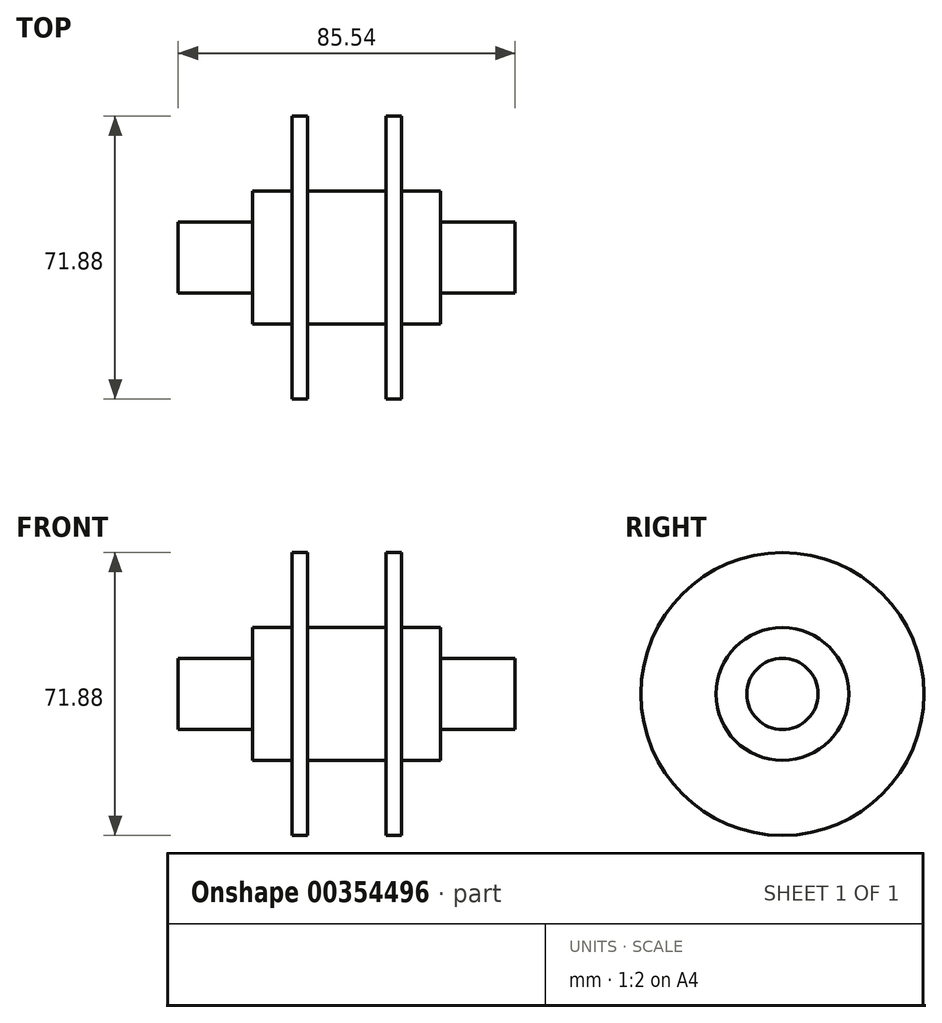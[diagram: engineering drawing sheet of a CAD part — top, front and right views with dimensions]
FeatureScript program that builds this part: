
annotation { "Feature Type Name" : "Feature", "Feature Type Description" : "" }
export const myFeature = defineFeature(function(context is Context, id is Id, definition is map)
    precondition{}
    {
        {
            var Q0;
            Q0=qCreatedBy(makeId("Front.planeOp"),FACE);
            var sketch = newSketch(context, id + "F0", { "sketchPlane" : qUnion([Q0])});
            skLineSegment(sketch, "E0", {"start": v(0, 0) * mm, "end": v(0, 16.87) * mm});
            skLineSegment(sketch, "E1", {"start": v(0, 16.87) * mm, "end": v(-9.98, 16.87) * mm});
            skLineSegment(sketch, "E2", {"start": v(-9.98, 16.87) * mm, "end": v(-9.98, 35.94) * mm});
            skLineSegment(sketch, "E3", {"start": v(-9.98, 35.94) * mm, "end": v(-13.9, 35.94) * mm});
            skLineSegment(sketch, "E4", {"start": v(-13.9, 35.94) * mm, "end": v(-13.9, 16.87) * mm});
            skLineSegment(sketch, "E5", {"start": v(-13.9, 16.87) * mm, "end": v(-23.88, 16.87) * mm});
            skLineSegment(sketch, "E6", {"start": v(-23.88, 16.87) * mm, "end": v(-23.88, 9.04) * mm});
            skLineSegment(sketch, "E7", {"start": v(-23.88, 9.04) * mm, "end": v(-42.77, 9.04) * mm});
            skLineSegment(sketch, "E8", {"start": v(-42.77, 9.04) * mm, "end": v(-42.77, 0) * mm});
            skLineSegment(sketch, "E9", {"start": v(-42.77, 0) * mm, "end": v(0, 0) * mm});
            skLineSegment(sketch, "E10.MirrorCS", {"start": v(0, 16.87) * mm, "end": v(9.98, 16.87) * mm});
            skLineSegment(sketch, "E11.MirrorCS", {"start": v(42.77, 0) * mm, "end": v(0, 0) * mm});
            skLineSegment(sketch, "E12.MirrorCS", {"start": v(42.77, 9.04) * mm, "end": v(42.77, 0) * mm});
            skLineSegment(sketch, "E13.MirrorCS", {"start": v(23.88, 9.04) * mm, "end": v(42.77, 9.04) * mm});
            skLineSegment(sketch, "E14.MirrorCS", {"start": v(13.9, 16.87) * mm, "end": v(23.88, 16.87) * mm});
            skLineSegment(sketch, "E15.MirrorCS", {"start": v(13.9, 35.94) * mm, "end": v(13.9, 16.87) * mm});
            skLineSegment(sketch, "E16.MirrorCS", {"start": v(9.98, 35.94) * mm, "end": v(13.9, 35.94) * mm});
            skLineSegment(sketch, "E17.MirrorCS", {"start": v(9.98, 16.87) * mm, "end": v(9.98, 35.94) * mm});
            skLineSegment(sketch, "E18.MirrorCS", {"start": v(23.88, 16.87) * mm, "end": v(23.88, 9.04) * mm});
            skSolve(sketch);
        }
        {
            var Q0;
            Q0=makeQuery(id+"F0.imprint","IMPRINT",FACE,{"disambiguationData":[TD([[makeQuery(id+"F0.imprint","IMPRINT",EDGE,{"derivedFrom":sQuery(id+"F0.wireOp",EDGE,"E0")}),1.0]])]});
            var Q1;
            Q1=makeQuery(id+"F0.imprint","IMPRINT",FACE,{"disambiguationData":[TD([[makeQuery(id+"F0.imprint","IMPRINT",EDGE,{"derivedFrom":sQuery(id+"F0.wireOp",EDGE,"E0")}),-1.0]])]});
            var Q2;
            Q2=sQuery(id+"F0.wireOp",EDGE,"E9");
            revolve(context, id + "F1", {"entities" : qUnion([Q0, Q1]), "axis" : qUnion([Q2]), "revolveType" : RevolveType.FULL});
        }
    });
